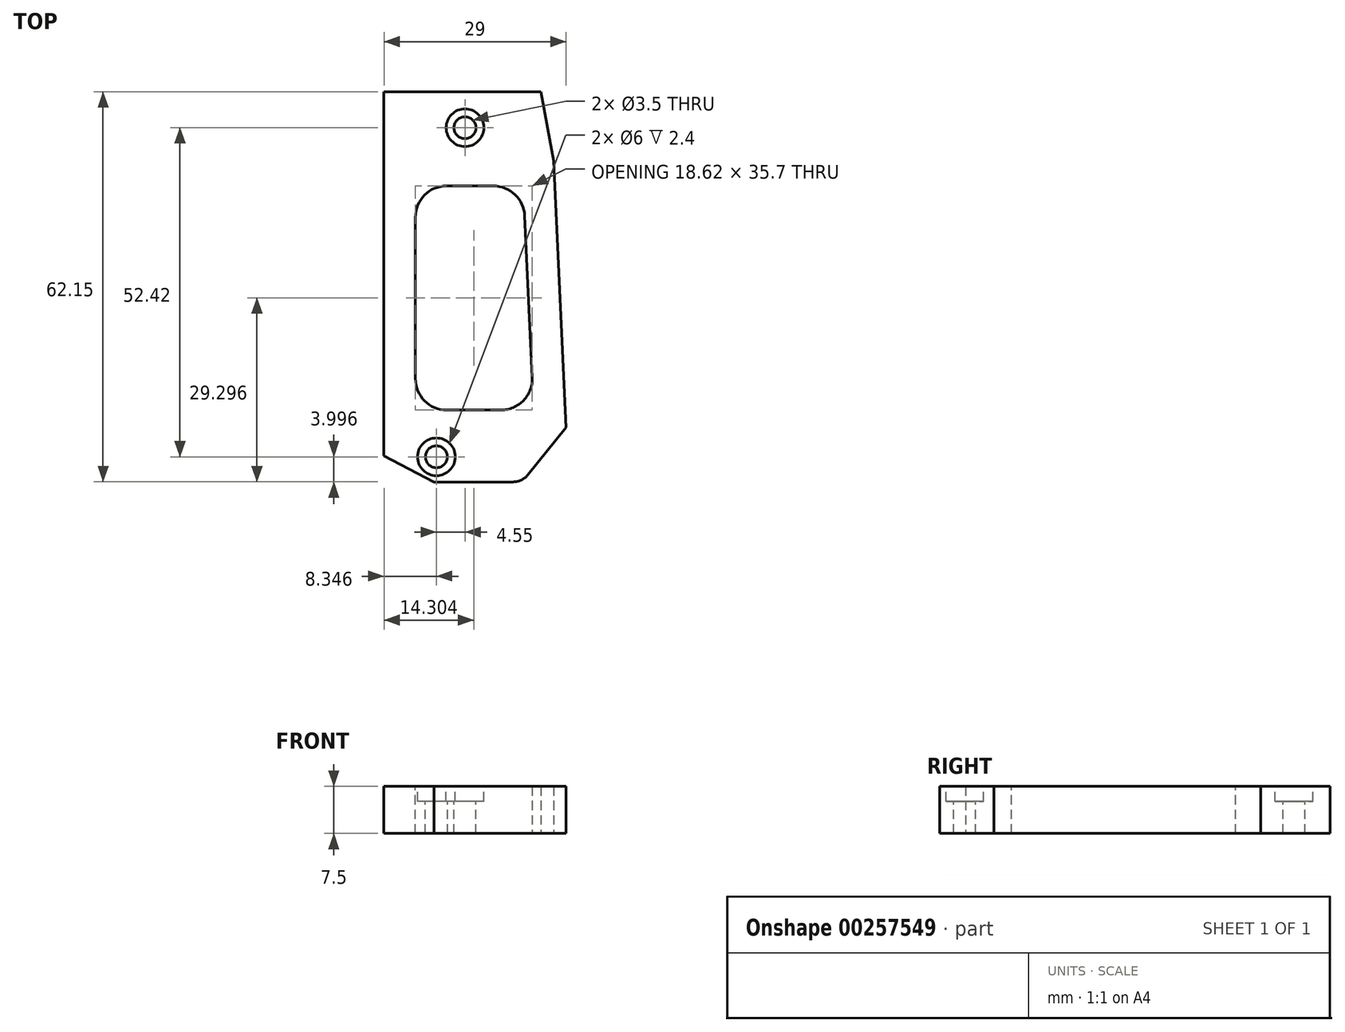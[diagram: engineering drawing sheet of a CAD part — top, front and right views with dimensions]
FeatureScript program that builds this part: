
annotation { "Feature Type Name" : "Feature", "Feature Type Description" : "" }
export const myFeature = defineFeature(function(context is Context, id is Id, definition is map)
    precondition{}
    {
        {
            var Q0;
            Q0=qCreatedBy(makeId("Top.planeOp"),FACE);
            var sketch = newSketch(context, id + "F0", { "sketchPlane" : qUnion([Q0])});
            skLineSegment(sketch, "E0", {"start": v(-17.95, 38.38) * mm, "end": v(7.05, 38.38) * mm});
            skLineSegment(sketch, "E1", {"start": v(7.05, 38.38) * mm, "end": v(9.05, 27.38) * mm});
            skLineSegment(sketch, "E2", {"start": v(9.05, 27.38) * mm, "end": v(11.05, -15.12) * mm});
            skLineSegment(sketch, "E3", {"start": v(11.05, -15.12) * mm, "end": v(4.05, -23.77) * mm});
            skLineSegment(sketch, "E4", {"start": v(4.05, -23.77) * mm, "end": v(-9.95, -23.77) * mm});
            skLineSegment(sketch, "E5", {"start": v(-9.95, -23.77) * mm, "end": v(-17.95, -19.62) * mm});
            skLineSegment(sketch, "E6", {"start": v(-17.95, -19.62) * mm, "end": v(-17.95, 38.38) * mm});
            skSolve(sketch);
        }
        {
            var Q0;
            Q0 = qSketchRegion(id + "F0", true);
            extrude(context, id + "F1", {"entities" : qUnion([Q0]), "depth" : 7.5 * mm});
        }
        {
            var Q0;
            Q0=makeQuery(id+"F1.opExtrude","CAP_FACE",FACE,{"disambiguationData":[OSD([sQuery(id+"F0.wireOp",EDGE,"E0"),sQuery(id+"F0.wireOp",EDGE,"E1"),sQuery(id+"F0.wireOp",EDGE,"E2"),sQuery(id+"F0.wireOp",EDGE,"E3"),sQuery(id+"F0.wireOp",EDGE,"E4"),sQuery(id+"F0.wireOp",EDGE,"E5"),sQuery(id+"F0.wireOp",EDGE,"E6")])],"isStart":false});
            var sketch = newSketch(context, id + "F2", { "sketchPlane" : qUnion([Q0])});
            skLineSegment(sketch, "E7", {"start": v(-12.95, 23.38) * mm, "end": v(-12.95, -12.32) * mm});
            skLineSegment(sketch, "E8", {"start": v(-12.95, -12.32) * mm, "end": v(5.9, -12.32) * mm});
            skLineSegment(sketch, "E9", {"start": v(5.9, -12.32) * mm, "end": v(4.23, 23.38) * mm});
            skLineSegment(sketch, "E10", {"start": v(4.23, 23.38) * mm, "end": v(-12.95, 23.38) * mm});
            skSolve(sketch);
        }
        {
            var Q0;
            Q0 = qSketchRegion(id + "F2", true);
            extrude(context, id + "F3", {"entities" : qUnion([Q0]), "operationType" : NewBodyOperationType.REMOVE, "endBound" : BoundingType.UP_TO_NEXT, "oppositeDirection" : true, "depth" : 25 * mm});
        }
        {
            var Q0;
            Q0=makeQuery(id+"F1.opExtrude","CAP_FACE",FACE,{"disambiguationData":[OSD([sQuery(id+"F0.wireOp",EDGE,"E0"),sQuery(id+"F0.wireOp",EDGE,"E1"),sQuery(id+"F0.wireOp",EDGE,"E2"),sQuery(id+"F0.wireOp",EDGE,"E3"),sQuery(id+"F0.wireOp",EDGE,"E4"),sQuery(id+"F0.wireOp",EDGE,"E5"),sQuery(id+"F0.wireOp",EDGE,"E6")])],"isStart":false});
            var sketch = newSketch(context, id + "F4", { "sketchPlane" : qUnion([Q0])});
            skCircle(sketch, "E11", {"center": v(-5.05, 32.65) * mm, "radius": 1.75 * mm});
            skCircle(sketch, "E12", {"center": v(-9.6, -19.77) * mm, "radius": 1.75 * mm});
            skSolve(sketch);
        }
        {
            var Q0;
            Q0 = qSketchRegion(id + "F4", true);
            extrude(context, id + "F5", {"entities" : qUnion([Q0]), "operationType" : NewBodyOperationType.REMOVE, "endBound" : BoundingType.UP_TO_NEXT, "oppositeDirection" : true, "depth" : 25 * mm});
        }
        {
            var Q0;
            Q0=makeQuery(id+"F1.opExtrude","CAP_FACE",FACE,{"disambiguationData":[OSD([sQuery(id+"F0.wireOp",EDGE,"E0"),sQuery(id+"F0.wireOp",EDGE,"E1"),sQuery(id+"F0.wireOp",EDGE,"E2"),sQuery(id+"F0.wireOp",EDGE,"E3"),sQuery(id+"F0.wireOp",EDGE,"E4"),sQuery(id+"F0.wireOp",EDGE,"E5"),sQuery(id+"F0.wireOp",EDGE,"E6")])],"isStart":false});
            var sketch = newSketch(context, id + "F6", { "sketchPlane" : qUnion([Q0])});
            skCircle(sketch, "E13", {"center": v(-5.05, 32.65) * mm, "radius": 3 * mm});
            skCircle(sketch, "E14", {"center": v(-9.6, -19.77) * mm, "radius": 3 * mm});
            skSolve(sketch);
        }
        {
            var Q0;
            Q0 = qSketchRegion(id + "F6", true);
            extrude(context, id + "F7", {"entities" : qUnion([Q0]), "operationType" : NewBodyOperationType.REMOVE, "oppositeDirection" : true, "depth" : 2.4 * mm});
        }
        {
            var Q0;
            Q0=makeQuery(id+"F1.opExtrude","SWEPT_EDGE",EDGE,{"disambiguationData":[OSD([sQuery(id+"F0.wireOp",EDGE,"E3"),sQuery(id+"F0.wireOp",EDGE,"E4")])]});
            fillet(context, id + "F8", {"entities" : qUnion([Q0]), "radius" : 3 * mm, "tangentPropagation" : true, "allowEdgeOverflow" : false});
        }
        {
            var Q0;
            Q0=makeQuery(id+"F3.boolean.opBoolean","COPY",EDGE,{"derivedFrom":makeQuery(id+"F3.opExtrude","SWEPT_EDGE",EDGE,{"disambiguationData":[OSD([sQuery(id+"F2.wireOp",EDGE,"E7"),sQuery(id+"F2.wireOp",EDGE,"E8")])]})});
            fillet(context, id + "F9", {"entities" : qUnion([Q0]), "radius" : 5 * mm, "tangentPropagation" : true, "allowEdgeOverflow" : false});
        }
        {
            var Q0;
            Q0=makeQuery(id+"F3.boolean.opBoolean","COPY",EDGE,{"derivedFrom":makeQuery(id+"F3.opExtrude","SWEPT_EDGE",EDGE,{"disambiguationData":[OSD([sQuery(id+"F2.wireOp",EDGE,"E8"),sQuery(id+"F2.wireOp",EDGE,"E9")])]})});
            fillet(context, id + "F10", {"entities" : qUnion([Q0]), "radius" : 5 * mm, "tangentPropagation" : true, "allowEdgeOverflow" : false});
        }
        {
            var Q0;
            Q0=makeQuery(id+"F3.boolean.opBoolean","COPY",EDGE,{"derivedFrom":makeQuery(id+"F3.opExtrude","SWEPT_EDGE",EDGE,{"disambiguationData":[OSD([sQuery(id+"F2.wireOp",EDGE,"E7"),sQuery(id+"F2.wireOp",EDGE,"E10")])]})});
            fillet(context, id + "F11", {"entities" : qUnion([Q0]), "radius" : 5 * mm, "tangentPropagation" : true, "allowEdgeOverflow" : false});
        }
        {
            var Q0;
            Q0=makeQuery(id+"F3.boolean.opBoolean","COPY",EDGE,{"derivedFrom":makeQuery(id+"F3.opExtrude","SWEPT_EDGE",EDGE,{"disambiguationData":[OSD([sQuery(id+"F2.wireOp",EDGE,"E9"),sQuery(id+"F2.wireOp",EDGE,"E10")])]})});
            fillet(context, id + "F12", {"entities" : qUnion([Q0]), "radius" : 5 * mm, "tangentPropagation" : true, "allowEdgeOverflow" : false});
        }
    });
